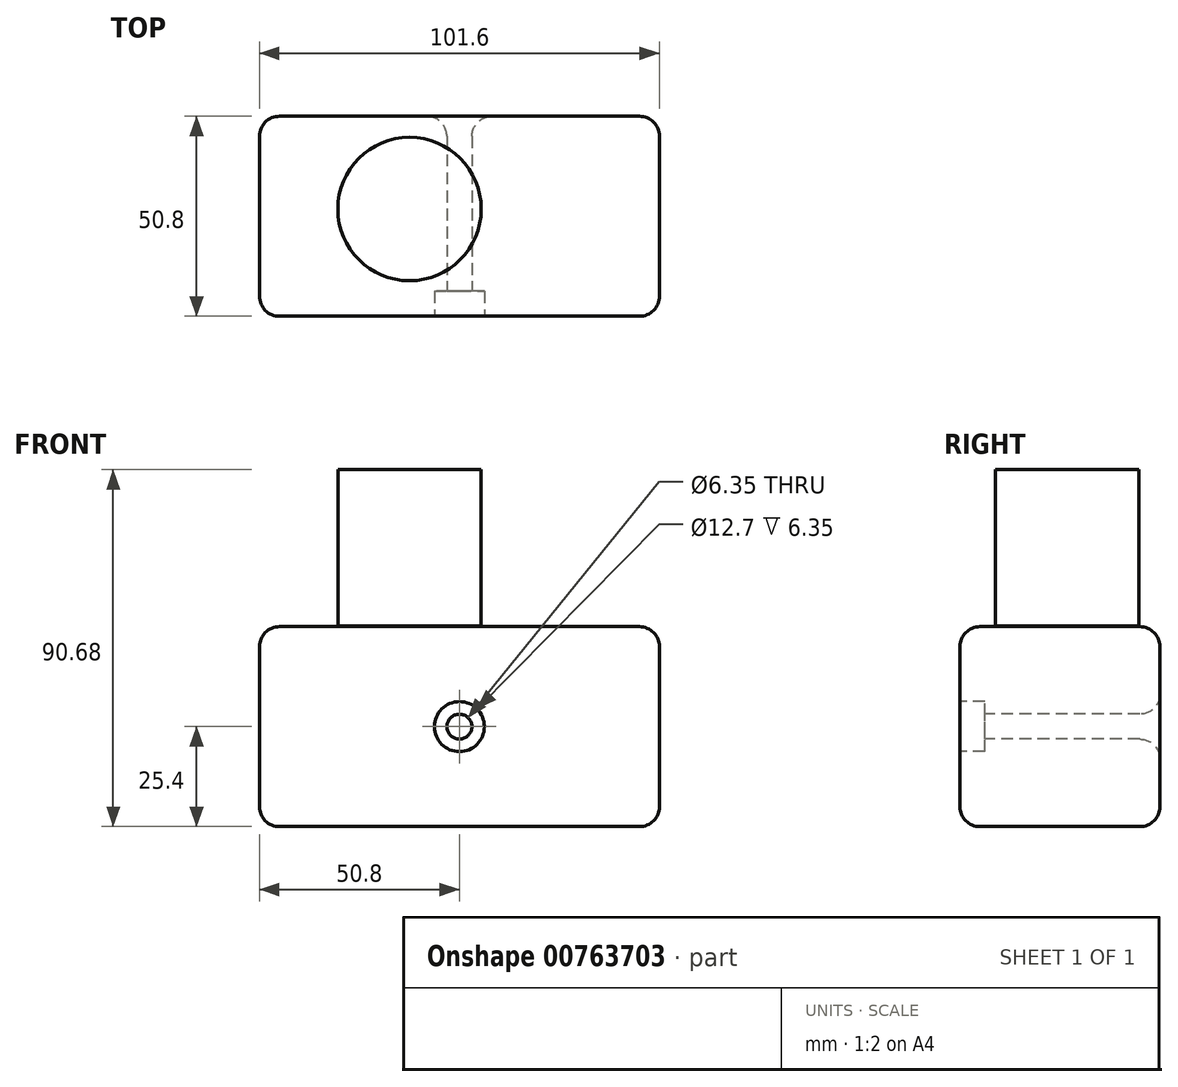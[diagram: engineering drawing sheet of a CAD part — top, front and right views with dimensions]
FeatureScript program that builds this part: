
annotation { "Feature Type Name" : "Feature", "Feature Type Description" : "" }
export const myFeature = defineFeature(function(context is Context, id is Id, definition is map)
    precondition{}
    {
        {
            var Q0;
            Q0=qCreatedBy(makeId("Top.planeOp"),FACE);
            var sketch = newSketch(context, id + "F0", { "sketchPlane" : qUnion([Q0])});
            skLineSegment(sketch, "E0.bottom", {"start": v(0, 0) * mm, "end": v(101.6, 0) * mm});
            skLineSegment(sketch, "E0.top", {"start": v(0, 50.8) * mm, "end": v(101.6, 50.8) * mm});
            skLineSegment(sketch, "E0.left", {"start": v(0, 0) * mm, "end": v(0, 50.8) * mm});
            skLineSegment(sketch, "E0.right", {"start": v(101.6, 0) * mm, "end": v(101.6, 50.8) * mm});
            skLineSegment(sketch, "E1.bottom", {"start": v(109.76, 0) * mm, "end": v(109.76, 0) * mm});
            skLineSegment(sketch, "E1.top", {"start": v(109.76, -4.34) * mm, "end": v(109.76, -4.34) * mm});
            skLineSegment(sketch, "E1.left", {"start": v(109.76, 0) * mm, "end": v(109.76, -4.34) * mm});
            skLineSegment(sketch, "E1.right", {"start": v(109.76, 0) * mm, "end": v(109.76, -4.34) * mm});
            skSolve(sketch);
        }
        {
            var Q0;
            Q0=makeQuery(id+"F0.imprint","IMPRINT",FACE,{"disambiguationData":[TD([[makeQuery(id+"F0.imprint","IMPRINT",EDGE,{"derivedFrom":sQuery(id+"F0.wireOp",EDGE,"E0.bottom")}),1.0]])]});
            extrude(context, id + "F1", {"entities" : qUnion([Q0]), "depth" : 50.8 * mm, "offsetDistance" : 25.4 * mm});
        }
        {
            var Q0;
            Q0=makeQuery(id+"F1.opExtrude","SWEPT_FACE",FACE,{"disambiguationData":[OSD([sQuery(id+"F0.wireOp",EDGE,"E0.bottom")])]});
            var sketch = newSketch(context, id + "F2", { "sketchPlane" : qUnion([Q0])});
            skPoint(sketch, "E2", {"position": v(50.8, 25.4) * mm});
            skSolve(sketch);
        }
        {
            var Q0;
            Q0=sQuery(id+"F2.wireOp",VERTEX,"E2");
            var Q1;
            Q1=makeQuery(id+"F1.opExtrude","SWEPT_BODY",BODY,{"disambiguationData":[OSD([sQuery(id+"F0.wireOp",EDGE,"E0.bottom"),sQuery(id+"F0.wireOp",EDGE,"E0.top"),sQuery(id+"F0.wireOp",EDGE,"E0.left"),sQuery(id+"F0.wireOp",EDGE,"E0.right")])]});
            hole(context, id + "F3", {"style" : HoleStyle.C_BORE, "endStyle" : HoleEndStyle.THROUGH, "holeDiameter" : 6.35 * mm, "cBoreDiameter" : 12.7 * mm, "cBoreDepth" : 6.35 * mm, "majorDiameter" : 6.35 * mm, "isTappedThrough" : true, "tappedDepth" : 12.7 * mm, "tapClearance" : 3, "locations" : qUnion([Q0]), "scope" : qUnion([Q1])});
        }
        {
            var Q0;
            Q0=makeQuery(id+"F1.opExtrude","CAP_EDGE",EDGE,{"disambiguationData":[OSD([sQuery(id+"F0.wireOp",EDGE,"E0.right")])],"isStart":false});
            var Q1;
            Q1=makeQuery(id+"F1.opExtrude","SWEPT_EDGE",EDGE,{"disambiguationData":[OSD([sQuery(id+"F0.wireOp",EDGE,"E0.bottom"),sQuery(id+"F0.wireOp",EDGE,"E0.right")])]});
            var Q2;
            Q2=makeQuery(id+"F1.opExtrude","SWEPT_EDGE",EDGE,{"disambiguationData":[OSD([sQuery(id+"F0.wireOp",EDGE,"E0.top"),sQuery(id+"F0.wireOp",EDGE,"E0.right")])]});
            var Q3;
            Q3=makeQuery(id+"F1.opExtrude","CAP_EDGE",EDGE,{"disambiguationData":[OSD([sQuery(id+"F0.wireOp",EDGE,"E0.right")])],"isStart":true});
            var Q4;
            Q4=makeQuery(id+"F1.opExtrude","CAP_EDGE",EDGE,{"disambiguationData":[OSD([sQuery(id+"F0.wireOp",EDGE,"E0.left")])],"isStart":false});
            var Q5;
            Q5=makeQuery(id+"F1.opExtrude","CAP_EDGE",EDGE,{"disambiguationData":[OSD([sQuery(id+"F0.wireOp",EDGE,"E0.left")])],"isStart":true});
            var Q6;
            Q6=makeQuery(id+"F1.opExtrude","SWEPT_EDGE",EDGE,{"disambiguationData":[OSD([sQuery(id+"F0.wireOp",EDGE,"E0.top"),sQuery(id+"F0.wireOp",EDGE,"E0.left")])]});
            var Q7;
            Q7=makeQuery(id+"F1.opExtrude","SWEPT_EDGE",EDGE,{"disambiguationData":[OSD([sQuery(id+"F0.wireOp",EDGE,"E0.bottom"),sQuery(id+"F0.wireOp",EDGE,"E0.left")])]});
            var Q8;
            Q8=makeQuery(id+"F1.opExtrude","CAP_EDGE",EDGE,{"disambiguationData":[OSD([sQuery(id+"F0.wireOp",EDGE,"E0.bottom")])],"isStart":false});
            var Q9;
            Q9=makeQuery(id+"F1.opExtrude","CAP_EDGE",EDGE,{"disambiguationData":[OSD([sQuery(id+"F0.wireOp",EDGE,"E0.bottom")])],"isStart":true});
            var Q10;
            Q10=makeQuery(id+"F1.opExtrude","SWEPT_FACE",FACE,{"disambiguationData":[OSD([sQuery(id+"F0.wireOp",EDGE,"E0.top")])]});
            var Q11;
            Q11=makeQuery(id+"F1.opExtrude","CAP_EDGE",EDGE,{"disambiguationData":[OSD([sQuery(id+"F0.wireOp",EDGE,"E0.top")])],"isStart":true});
            fillet(context, id + "F4", {"entities" : qUnion([Q0, Q1, Q2, Q3, Q4, Q5, Q6, Q7, Q8, Q9, Q10, Q11]), "radius" : 5.08 * mm, "tangentPropagation" : true, "allowEdgeOverflow" : false});
        }
        {
            var Q0;
            Q0=makeQuery(id+"F1.opExtrude","CAP_FACE",FACE,{"disambiguationData":[OSD([sQuery(id+"F0.wireOp",EDGE,"E0.bottom"),sQuery(id+"F0.wireOp",EDGE,"E0.top"),sQuery(id+"F0.wireOp",EDGE,"E0.left"),sQuery(id+"F0.wireOp",EDGE,"E0.right")])],"isStart":false});
            cPlane(context, id + "F5", {"entities" : qUnion([Q0]), "cplaneType" : CPlaneType.OFFSET, "offset" : 39.88 * mm, "width" : 152.4 * mm, "height" : 152.4 * mm});
        }
        {
            var Q0;
            Q0=qCreatedBy(id+"F5.planeOp",FACE);
            var sketch = newSketch(context, id + "F6", { "sketchPlane" : qUnion([Q0])});
            skCircle(sketch, "E3", {"center": v(38.13, 27.23) * mm, "radius": 18.22 * mm});
            skSolve(sketch);
        }
        {
            var Q0;
            Q0=makeQuery(id+"F6.imprint","IMPRINT",FACE,{"disambiguationData":[TD([[makeQuery(id+"F6.imprint","IMPRINT",EDGE,{"derivedFrom":sQuery(id+"F6.wireOp",EDGE,"E3")}),1.0]])]});
            extrude(context, id + "F7", {"entities" : qUnion([Q0]), "oppositeDirection" : true, "depth" : 39.75 * mm, "offsetDistance" : 25.4 * mm});
        }
    });
